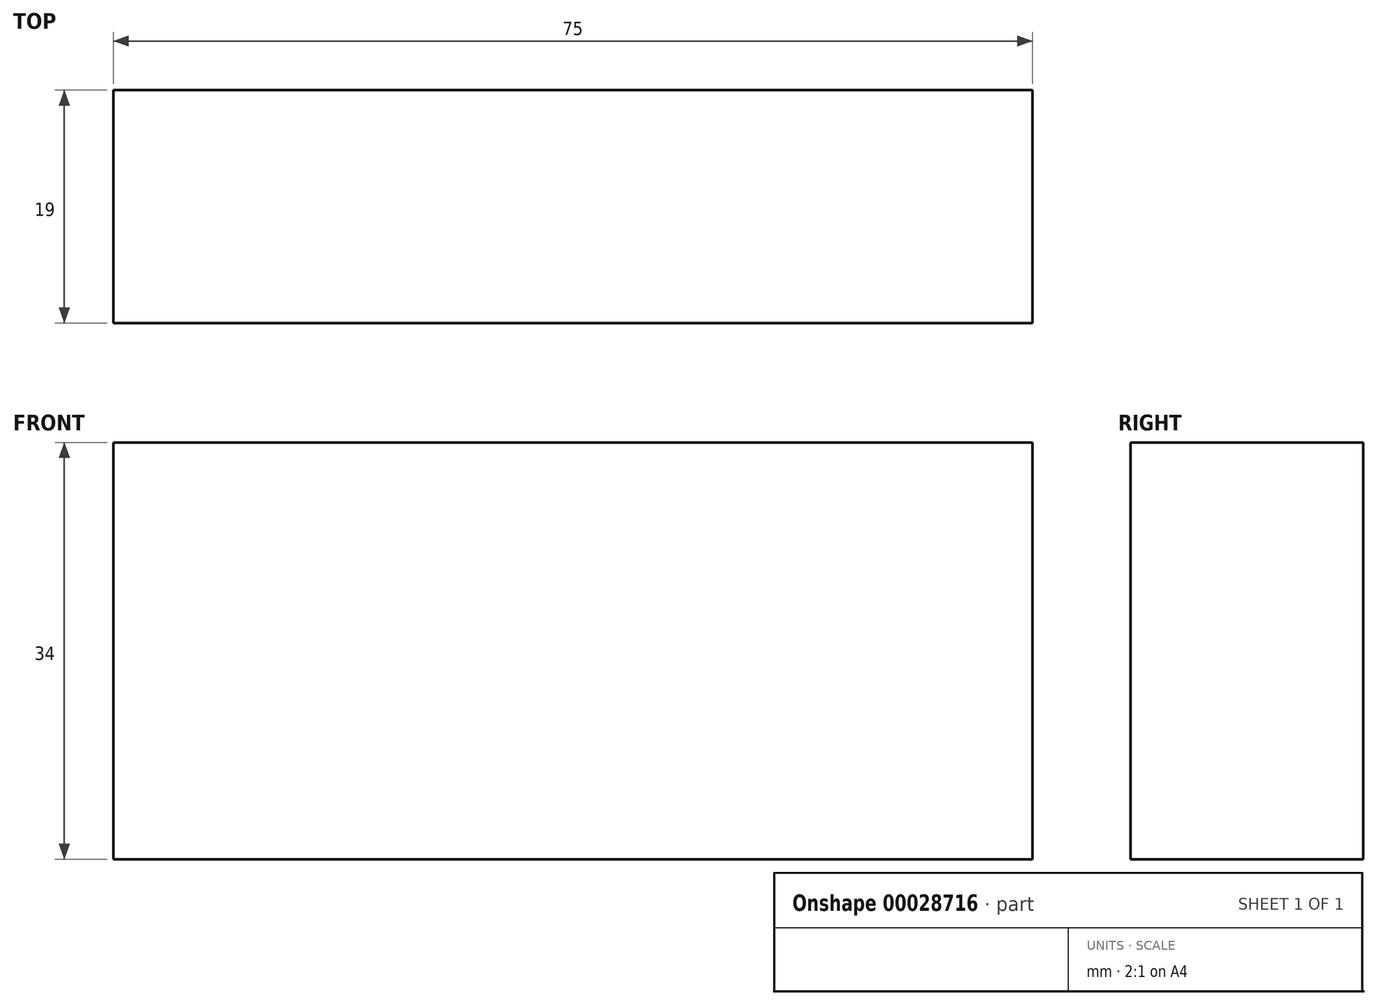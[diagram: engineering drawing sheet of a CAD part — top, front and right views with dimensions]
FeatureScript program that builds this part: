
annotation { "Feature Type Name" : "Feature", "Feature Type Description" : "" }
export const myFeature = defineFeature(function(context is Context, id is Id, definition is map)
    precondition{}
    {
        {
            var Q0;
            Q0=qCreatedBy(makeId("Front.planeOp"),FACE);
            var sketch = newSketch(context, id + "F0", { "sketchPlane" : qUnion([Q0])});
            skLineSegment(sketch, "E0.bottom", {"start": v(-37.5, 17) * mm, "end": v(37.5, 17) * mm});
            skLineSegment(sketch, "E0.top", {"start": v(-37.5, -17) * mm, "end": v(37.5, -17) * mm});
            skLineSegment(sketch, "E0.left", {"start": v(-37.5, 17) * mm, "end": v(-37.5, -17) * mm});
            skLineSegment(sketch, "E0.right", {"start": v(37.5, 17) * mm, "end": v(37.5, -17) * mm});
            skPoint(sketch, "E0.middle", {"position": v(0, 0) * mm});
            skSolve(sketch);
        }
        {
            var Q0;
            Q0 = qSketchRegion(id + "F0", true);
            extrude(context, id + "F1", {"entities" : qUnion([Q0]), "endBound" : BoundingType.SYMMETRIC, "depth" : 19 * mm, "offsetDistance" : 25 * mm});
        }
    });
